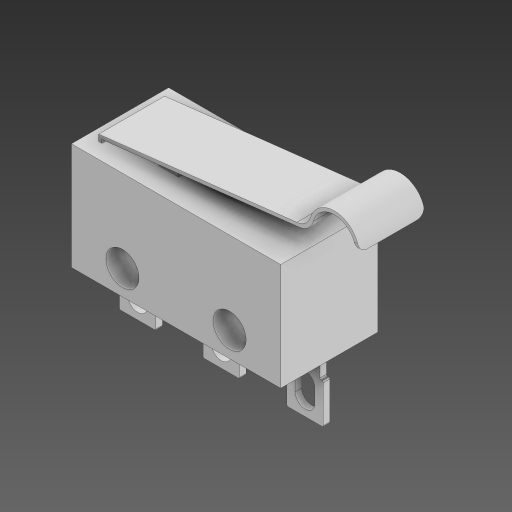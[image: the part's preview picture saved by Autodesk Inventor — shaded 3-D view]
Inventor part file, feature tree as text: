
AUTODESK INVENTOR PART (.ipt)
format: ipt  version: 2024 (Build 280153000, 153)  size: 256,000 bytes
history: native  units: mm
features: extrude x4, sketch x4, fillet x3, plane x1, pattern_linear x1
ambient origin geometry x8: Origin, YZ Plane, XZ Plane, XY Plane, X Axis, Y Axis, Z Axis, Center Point
bodies: Solid1 (feature_tree)
feature tree (13):
  extrude  "Extrusion1"  Depth=6.5mm
  plane  "Work Plane1"
  extrude  "Extrusion2"  Depth=2.0mm
  extrude  "Extrusion3"  Depth=3.25mm
  fillet  "Fillet1"  Radius=6.5mm
  pattern_linear  "Rectangular Pattern1"  Spacing1=2.2mm  [1 undecoded]
  extrude  "Extrusion4"  Depth=0.5mm TaperAngle=0.0deg
  fillet  "Fillet2"  Radius=1.2mm
  fillet  "Fillet3"  Radius=5.2mm
  sketch  "Sketch1"  dims[d0=12.7mm d1=6.5mm]
  sketch  "Sketch2"  dims[d2=2.0mm d3=2.0mm]
  sketch  "Sketch3"  dims[d4=1.5mm d5=3.25mm d6=6.5mm]
  sketch  "Sketch4"  dims[d7=5.9mm d8=0.0mm d13=2.2mm d15=0.4mm d16=0.0mm d17=1.2mm d18=5.2mm d19=2.9mm d20=0.0mm d21=0.8mm d22=0.6mm d23=1.0mm d24=1.8mm d27=5.08mm d28=1.1mm d29=3.5mm d37=0.075mm d38=30.0mm d40=5.08mm d43=15.0mm d44=10.0mm d45=0.2mm d47=0.8mm d49=3.0mm d50=0.2mm d51=0.2mm d52=0.2mm d53=4.0mm d54=0.0mm d55=1.0mm d56=0.5mm]
note: 1 required parameter value undecoded (feature->parameter linkage not recoverable at this tier; creation-order binding heuristic only, values carry confidence <= 0.55)
